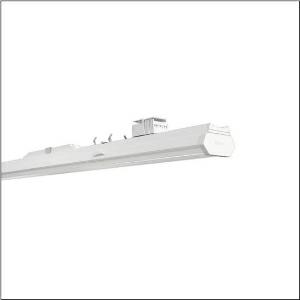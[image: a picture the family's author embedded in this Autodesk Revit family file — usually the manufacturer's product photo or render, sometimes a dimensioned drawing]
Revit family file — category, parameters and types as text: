
# Revit family: licross_r__11_protected_mo_51tp12mn4axg_95e7
name_source: partatom
category: Lighting Fixtures
units: mm (PartAtom-declared; Revit-internal decimal feet)

## family parameters
Cut with Voids When Loaded = No
Host = Face
Light Source = No
Part Type = Normal
Room Calculation Point = No
Round Connector Dimension = Use Diameter
Shared = No

## types (1)
- --- (1 x LED, 10020 lm, 55.3 W, 4000K)
    Apparent Load = 55 VA
    CIE Flux Codes = 73 92 98 99 100
    Color Rendering = 80
    Color Temperature = 4000K
    Default Elevation = 1800 mm
    Description = Licross® 11 Protected MO, luminaire insert, of sheet steel, galvanised, coil coated, white, length: 1.500mm, width: 90mm, height: 101mm, LED rated luminous flux: 10.030lm, light colour: 840, control gear: ON/OFF Multilumen, with plug, 3-pole, with phase selection, mains connection: 220..240V, AC, 50/60Hz, rated input power: 55W, halogen-free wiring, primary light control with lens, of plastic, primary optical cover: cover, of PMMA, light emission: direct distribution, primary light characteristic: symmetric, protection rating (complete): IP64, insulation class (complete): insulation class I (protective earthing), certification: CE, ENEC, VDE, UKCA, protection symbol: D if used in an environment with conductive dust loads with corresponding accessories, impact resistance: IK06, permissible ambient temperature for indoor applications: -35..+40°C, corresponds to IFS (International Featured Standards) requirements for safety and quality in the food industry, reducing of maximum allowable ambient temperature of 5°C with ceiling mounting, LABS conformity tested according to VDMA 24364:2018-05, packaging unit: 1 piece
    Height = 92 mm
    Lamp = 1 x LED
    Lamp Light Flux = 10020 lm
    Lamp Power = 55.3 W
    Lamp count = 1
    Length = 1500 mm
    Luminous efficacy = 181 lm/W
    Manufacturer = Siteco
    ModVariant = No
    Model = 51TP12MN4AXG
    Mounting Place = Ceiling
    Mounting Type = Pendant
    Number of Poles = 1
    OnlyDefault = Yes
    Power Factor = 1
    Product Name = Licross® 11 Protected MO
    Product group = luminaire insert
    ProductGroupID = 902
    Protection Class = Protection class I
    Protection Degree = IP 64
    RLX_Detail_Level = 1
    RLX_Emergency_Light_Flux = 0 lm
    RLX_Emergency_Type = 0
    RLX_Emergency_Type_DB = No
    RlxData = <blob elided: 22113 chars, md5=291907e6>
    Socket = socket
    Standby Power = 0 W
    System Light Flux = 10020 lm
    System Power = 55 W
    Type Comments = factory setting: luminous flux: 100 % | (A | C | E) | 126 mA
    Type Image = l_1256148.jpg
    URL = http://relux.com
    VarID = @adj_085906
    Voltage = 0 V
    Weight = 0.00 kg
    Width = 88 mm

## geometry (parser evidence)
native form markers: Blend x4, Sweep x9
no freeform markers — native parametric forms only
